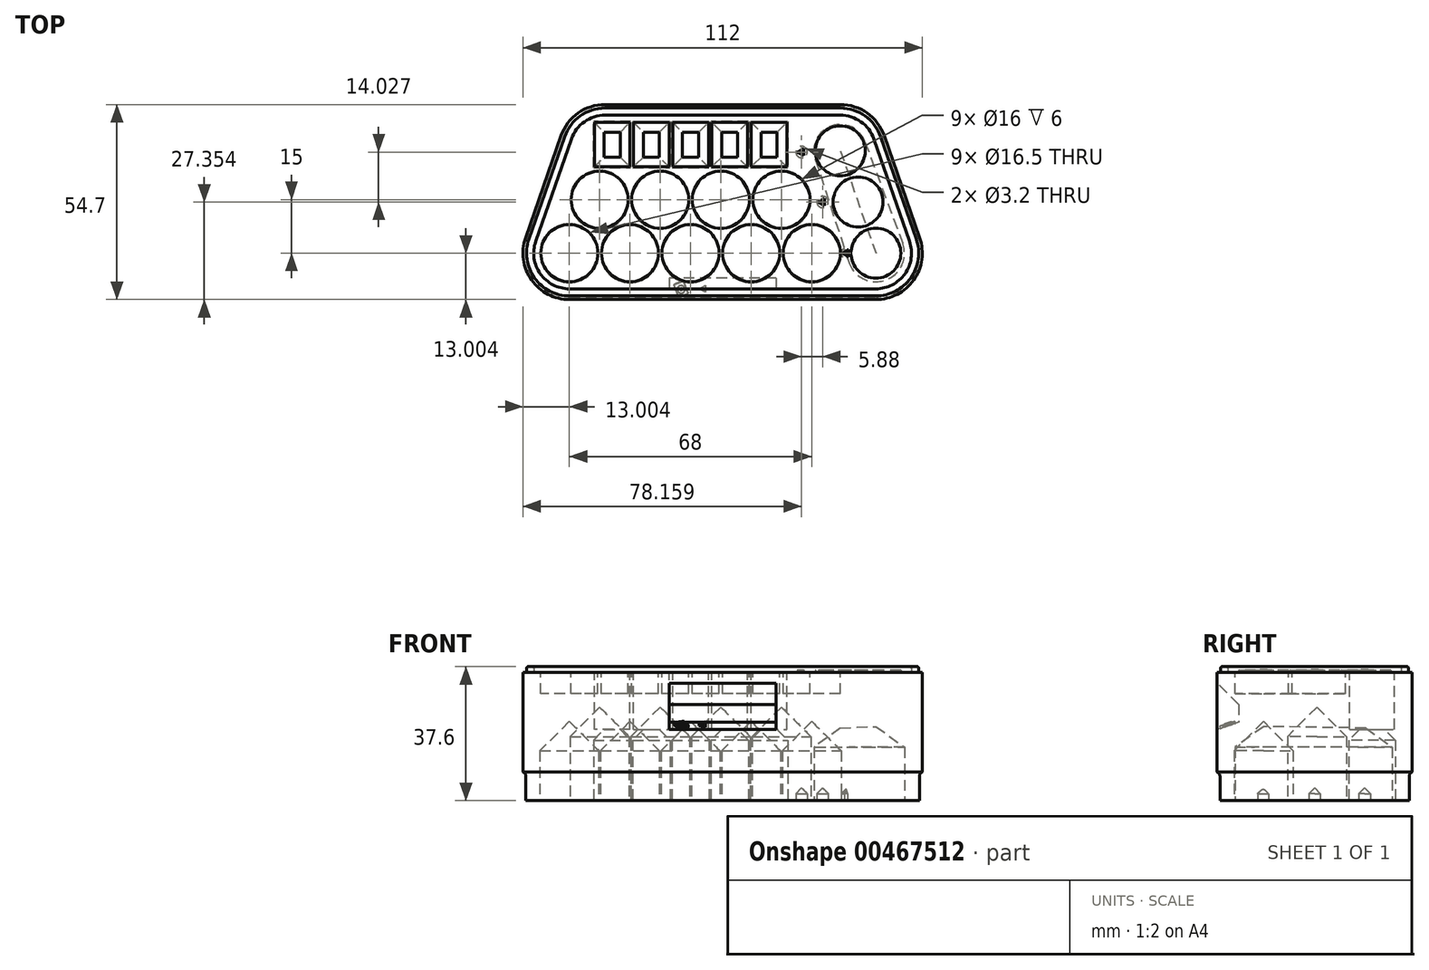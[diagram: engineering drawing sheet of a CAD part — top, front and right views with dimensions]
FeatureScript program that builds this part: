
annotation { "Feature Type Name" : "Feature", "Feature Type Description" : "" }
export const myFeature = defineFeature(function(context is Context, id is Id, definition is map)
    precondition{}
    {
        {
            var Q0;
            Q0=qCreatedBy(makeId("Top.planeOp"),FACE);
            var sketch = newSketch(context, id + "F0", { "sketchPlane" : qUnion([Q0])});
            skLineSegment(sketch, "E0", {"start": v(-9.05, 12.46) * mm, "end": v(-26.05, 12.46) * mm, "construction": true});
            skLineSegment(sketch, "E1", {"start": v(-26.05, 12.46) * mm, "end": v(-43.05, 12.46) * mm, "construction": true});
            skLineSegment(sketch, "E2", {"start": v(-9.05, 12.46) * mm, "end": v(7.95, 12.46) * mm, "construction": true});
            skLineSegment(sketch, "E3", {"start": v(7.95, 12.46) * mm, "end": v(24.95, 12.46) * mm, "construction": true});
            skLineSegment(sketch, "E4", {"start": v(-34.55, 27.46) * mm, "end": v(-17.55, 27.46) * mm, "construction": true});
            skPoint(sketch, "E4.endSnap0", {"position": v(-17.55, 12.46) * mm});
            skLineSegment(sketch, "E5", {"start": v(-17.55, 27.46) * mm, "end": v(-0.55, 27.46) * mm, "construction": true});
            skPoint(sketch, "E5.endSnap0", {"position": v(-0.55, 12.46) * mm});
            skLineSegment(sketch, "E6", {"start": v(-0.55, 27.46) * mm, "end": v(16.45, 27.46) * mm, "construction": true});
            skPoint(sketch, "E6.endSnap0", {"position": v(16.45, 12.46) * mm});
            skCircle(sketch, "E7", {"center": v(-43.05, 12.46) * mm, "radius": 8 * mm});
            skCircle(sketch, "E8", {"center": v(-26.05, 12.46) * mm, "radius": 8 * mm});
            skCircle(sketch, "E9", {"center": v(-9.05, 12.46) * mm, "radius": 8 * mm});
            skCircle(sketch, "E10", {"center": v(7.95, 12.46) * mm, "radius": 8 * mm});
            skCircle(sketch, "E11", {"center": v(24.95, 12.46) * mm, "radius": 8 * mm});
            skCircle(sketch, "E12", {"center": v(-34.55, 27.46) * mm, "radius": 8 * mm});
            skCircle(sketch, "E13", {"center": v(-17.55, 27.46) * mm, "radius": 8 * mm});
            skCircle(sketch, "E14", {"center": v(-0.55, 27.46) * mm, "radius": 8 * mm});
            skCircle(sketch, "E15", {"center": v(16.45, 27.46) * mm, "radius": 8 * mm});
            skLineSegment(sketch, "E16.top", {"start": v(-26.05, 49.16) * mm, "end": v(-36.05, 49.16) * mm});
            skLineSegment(sketch, "E16.left", {"start": v(-26.05, 36.66) * mm, "end": v(-26.05, 49.16) * mm});
            skLineSegment(sketch, "E16.right", {"start": v(-36.05, 36.66) * mm, "end": v(-36.05, 49.16) * mm});
            skArc(sketch, "E17", {"start": v(-55.32, 16.74) * mm, "mid": v(-53.64, 4.93) * mm, "end": v(-43.05, -0.54) * mm});
            skLineSegment(sketch, "E18", {"start": v(-45.32, 45.44) * mm, "end": v(-55.32, 16.74) * mm});
            skLineSegment(sketch, "E19", {"start": v(-43.05, -0.54) * mm, "end": v(42.95, -0.54) * mm});
            skLineSegment(sketch, "E20", {"start": v(32.95, 54.16) * mm, "end": v(-33.05, 54.16) * mm});
            skArc(sketch, "E21.trimOffspring", {"start": v(-33.05, 54.16) * mm, "mid": v(-40.58, 51.76) * mm, "end": v(-45.32, 45.44) * mm});
            skLineSegment(sketch, "E22", {"start": v(-43.05, 12.46) * mm, "end": v(-43.05, 19.46) * mm, "construction": true});
            skLineSegment(sketch, "E23", {"start": v(-36.05, 36.66) * mm, "end": v(-26.05, 36.66) * mm});
            skLineSegment(sketch, "E24", {"start": v(-34.55, 19.46) * mm, "end": v(16.45, 19.46) * mm, "construction": true});
            skLineSegment(sketch, "E25", {"start": v(-43.05, 20.46) * mm, "end": v(24.95, 20.46) * mm, "construction": true});
            skLineSegment(sketch, "E26", {"start": v(-26.05, 49.16) * mm, "end": v(-25.05, 49.16) * mm, "construction": true});
            skLineSegment(sketch, "E27.bottom", {"start": v(-25.05, 49.16) * mm, "end": v(-15.05, 49.16) * mm});
            skLineSegment(sketch, "E27.top", {"start": v(-25.05, 36.66) * mm, "end": v(-15.05, 36.66) * mm});
            skLineSegment(sketch, "E27.left", {"start": v(-25.05, 49.16) * mm, "end": v(-25.05, 36.66) * mm});
            skLineSegment(sketch, "E27.right", {"start": v(-15.05, 49.16) * mm, "end": v(-15.05, 36.66) * mm});
            skLineSegment(sketch, "E28", {"start": v(-15.05, 49.16) * mm, "end": v(-14.05, 49.16) * mm, "construction": true});
            skLineSegment(sketch, "E29.bottom", {"start": v(-14.05, 49.16) * mm, "end": v(-4.05, 49.16) * mm});
            skLineSegment(sketch, "E29.top", {"start": v(-14.05, 36.66) * mm, "end": v(-4.05, 36.66) * mm});
            skLineSegment(sketch, "E29.left", {"start": v(-14.05, 49.16) * mm, "end": v(-14.05, 36.66) * mm});
            skLineSegment(sketch, "E29.right", {"start": v(-4.05, 49.16) * mm, "end": v(-4.05, 36.66) * mm});
            skLineSegment(sketch, "E30", {"start": v(-4.05, 49.16) * mm, "end": v(-3.05, 49.16) * mm, "construction": true});
            skLineSegment(sketch, "E31.left", {"start": v(-3.05, 49.16) * mm, "end": v(-3.05, 36.66) * mm});
            skLineSegment(sketch, "E31.right", {"start": v(7.95, 49.16) * mm, "end": v(7.95, 36.66) * mm});
            skLineSegment(sketch, "E32.left", {"start": v(6.95, 49.16) * mm, "end": v(6.95, 36.66) * mm});
            skLineSegment(sketch, "E32.right", {"start": v(17.95, 49.16) * mm, "end": v(17.95, 36.66) * mm});
            skLineSegment(sketch, "E33", {"start": v(-3.05, 36.66) * mm, "end": v(6.95, 36.66) * mm});
            skLineSegment(sketch, "E34", {"start": v(7.95, 36.66) * mm, "end": v(17.95, 36.66) * mm});
            skPoint(sketch, "E35", {"position": v(-9.05, 49.16) * mm});
            skLineSegment(sketch, "E36", {"start": v(7.95, 49.16) * mm, "end": v(17.95, 49.16) * mm});
            skLineSegment(sketch, "E37", {"start": v(6.95, 49.16) * mm, "end": v(-3.05, 49.16) * mm});
            skLineSegment(sketch, "E38", {"start": v(6.95, 49.16) * mm, "end": v(7.95, 49.16) * mm, "construction": true});
            skLineSegment(sketch, "E39", {"start": v(45.23, 45.44) * mm, "end": v(55.23, 16.74) * mm});
            skArc(sketch, "E40.trimOffspring", {"start": v(45.23, 45.44) * mm, "mid": v(40.48, 51.76) * mm, "end": v(32.95, 54.16) * mm});
            skArc(sketch, "E41.trimOffspring", {"start": v(42.95, -0.54) * mm, "mid": v(53.55, 4.93) * mm, "end": v(55.23, 16.74) * mm});
            skLineSegment(sketch, "E42", {"start": v(-34.55, 27.46) * mm, "end": v(-34.55, 35.46) * mm, "construction": true});
            skLineSegment(sketch, "E43", {"start": v(-34.55, 35.46) * mm, "end": v(-34.55, 36.66) * mm, "construction": true});
            skLineSegment(sketch, "E44", {"start": v(-33.05, 41.16) * mm, "end": v(14.95, 41.16) * mm, "construction": true});
            skLineSegment(sketch, "E45", {"start": v(-9.05, 41.16) * mm, "end": v(-9.05, 12.46) * mm, "construction": true});
            skCircle(sketch, "E46", {"center": v(42.95, 12.46) * mm, "radius": 7 * mm});
            skCircle(sketch, "E47", {"center": v(32.95, 41.16) * mm, "radius": 7 * mm});
            skPoint(sketch, "E47.centerSnap0", {"position": v(17.95, 42.91) * mm});
            skLineSegment(sketch, "E48", {"start": v(32.95, 41.16) * mm, "end": v(42.95, 12.46) * mm, "construction": true});
            skCircle(sketch, "E49", {"center": v(37.95, 26.81) * mm, "radius": 7 * mm});
            skLineSegment(sketch, "E50", {"start": v(42.95, 12.46) * mm, "end": v(32.95, 12.46) * mm, "construction": true});
            skLineSegment(sketch, "E51", {"start": v(27.95, 40.84) * mm, "end": v(17.95, 40.84) * mm, "construction": true});
            skLineSegment(sketch, "E52", {"start": v(20.95, 40.84) * mm, "end": v(22.69, 41.84) * mm});
            skLineSegment(sketch, "E53", {"start": v(22.69, 41.84) * mm, "end": v(22.69, 39.84) * mm});
            skLineSegment(sketch, "E54", {"start": v(22.69, 39.84) * mm, "end": v(20.95, 40.84) * mm});
            skLineSegment(sketch, "E55", {"start": v(26.83, 26.81) * mm, "end": v(28.57, 27.81) * mm});
            skLineSegment(sketch, "E56", {"start": v(28.57, 27.81) * mm, "end": v(28.57, 25.81) * mm});
            skLineSegment(sketch, "E57", {"start": v(28.57, 25.81) * mm, "end": v(26.83, 26.81) * mm});
            skLineSegment(sketch, "E58", {"start": v(33.7, 12.46) * mm, "end": v(35.44, 13.46) * mm});
            skLineSegment(sketch, "E59", {"start": v(35.44, 13.46) * mm, "end": v(35.44, 11.46) * mm});
            skLineSegment(sketch, "E60", {"start": v(35.44, 11.46) * mm, "end": v(33.7, 12.46) * mm});
            skLineSegment(sketch, "E61", {"start": v(-55.32, 16.74) * mm, "end": v(-55.32, 45.44) * mm, "construction": true});
            skLineSegment(sketch, "E62", {"start": v(-55.32, 45.44) * mm, "end": v(-45.32, 45.44) * mm, "construction": true});
            skLineSegment(sketch, "E63", {"start": v(45.23, 45.44) * mm, "end": v(55.23, 45.44) * mm, "construction": true});
            skLineSegment(sketch, "E64", {"start": v(55.23, 45.44) * mm, "end": v(55.23, 16.74) * mm, "construction": true});
            skLineSegment(sketch, "E65", {"start": v(-43.05, -0.54) * mm, "end": v(-43.05, 4.46) * mm, "construction": true});
            skSolve(sketch);
        }
        {
            var Q0;
            Q0=makeQuery(id+"F0.imprint","IMPRINT",FACE,{"disambiguationData":[TD([[makeQuery(id+"F0.imprint","IMPRINT",EDGE,{"derivedFrom":sQuery(id+"F0.wireOp",EDGE,"E12")}),1.0]])]});
            var Q1;
            Q1=makeQuery(id+"F0.imprint","IMPRINT",FACE,{"disambiguationData":[TD([[makeQuery(id+"F0.imprint","IMPRINT",EDGE,{"derivedFrom":sQuery(id+"F0.wireOp",EDGE,"E13")}),1.0]])]});
            var Q2;
            Q2=makeQuery(id+"F0.imprint","IMPRINT",FACE,{"disambiguationData":[TD([[makeQuery(id+"F0.imprint","IMPRINT",EDGE,{"derivedFrom":sQuery(id+"F0.wireOp",EDGE,"E14")}),1.0]])]});
            var Q3;
            Q3=makeQuery(id+"F0.imprint","IMPRINT",FACE,{"disambiguationData":[TD([[makeQuery(id+"F0.imprint","IMPRINT",EDGE,{"derivedFrom":sQuery(id+"F0.wireOp",EDGE,"E15")}),1.0]])]});
            var Q4;
            Q4=makeQuery(id+"F0.imprint","IMPRINT",FACE,{"disambiguationData":[TD([[makeQuery(id+"F0.imprint","IMPRINT",EDGE,{"derivedFrom":sQuery(id+"F0.wireOp",EDGE,"E31.right")}),1.0]])]});
            var Q5;
            Q5=makeQuery(id+"F0.imprint","IMPRINT",FACE,{"disambiguationData":[TD([[makeQuery(id+"F0.imprint","IMPRINT",EDGE,{"derivedFrom":sQuery(id+"F0.wireOp",EDGE,"E31.left")}),1.0]])]});
            var Q6;
            Q6=makeQuery(id+"F0.imprint","IMPRINT",FACE,{"disambiguationData":[TD([[makeQuery(id+"F0.imprint","IMPRINT",EDGE,{"derivedFrom":sQuery(id+"F0.wireOp",EDGE,"E29.bottom")}),-1.0]])]});
            var Q7;
            Q7=makeQuery(id+"F0.imprint","IMPRINT",FACE,{"disambiguationData":[TD([[makeQuery(id+"F0.imprint","IMPRINT",EDGE,{"derivedFrom":sQuery(id+"F0.wireOp",EDGE,"E27.bottom")}),-1.0]])]});
            var Q8;
            Q8=makeQuery(id+"F0.imprint","IMPRINT",FACE,{"disambiguationData":[TD([[makeQuery(id+"F0.imprint","IMPRINT",EDGE,{"derivedFrom":sQuery(id+"F0.wireOp",EDGE,"E16.top")}),1.0]])]});
            var Q9;
            Q9=makeQuery(id+"F0.imprint","IMPRINT",FACE,{"disambiguationData":[TD([[makeQuery(id+"F0.imprint","IMPRINT",EDGE,{"derivedFrom":sQuery(id+"F0.wireOp",EDGE,"E8")}),1.0]])]});
            var Q10;
            Q10=makeQuery(id+"F0.imprint","IMPRINT",FACE,{"disambiguationData":[TD([[makeQuery(id+"F0.imprint","IMPRINT",EDGE,{"derivedFrom":sQuery(id+"F0.wireOp",EDGE,"E9")}),1.0]])]});
            var Q11;
            Q11=makeQuery(id+"F0.imprint","IMPRINT",FACE,{"disambiguationData":[TD([[makeQuery(id+"F0.imprint","IMPRINT",EDGE,{"derivedFrom":sQuery(id+"F0.wireOp",EDGE,"E10")}),1.0]])]});
            var Q12;
            Q12=makeQuery(id+"F0.imprint","IMPRINT",FACE,{"disambiguationData":[TD([[makeQuery(id+"F0.imprint","IMPRINT",EDGE,{"derivedFrom":sQuery(id+"F0.wireOp",EDGE,"E11")}),1.0]])]});
            var Q13;
            Q13=makeQuery(id+"F0.imprint","IMPRINT",FACE,{"disambiguationData":[TD([[makeQuery(id+"F0.imprint","IMPRINT",EDGE,{"derivedFrom":sQuery(id+"F0.wireOp",EDGE,"E7")}),1.0]])]});
            var Q14;
            Q14=makeQuery(id+"F0.imprint","IMPRINT",FACE,{"disambiguationData":[TD([[makeQuery(id+"F0.imprint","IMPRINT",EDGE,{"derivedFrom":sQuery(id+"F0.wireOp",EDGE,"E47")}),1.0]])]});
            var Q15;
            Q15=makeQuery(id+"F0.imprint","IMPRINT",FACE,{"disambiguationData":[TD([[makeQuery(id+"F0.imprint","IMPRINT",EDGE,{"derivedFrom":sQuery(id+"F0.wireOp",EDGE,"E49")}),1.0]])]});
            var Q16;
            Q16=makeQuery(id+"F0.imprint","IMPRINT",FACE,{"disambiguationData":[TD([[makeQuery(id+"F0.imprint","IMPRINT",EDGE,{"derivedFrom":sQuery(id+"F0.wireOp",EDGE,"E46")}),1.0]])]});
            var Q17;
            Q17=makeQuery(id+"F0.imprint","IMPRINT",FACE,{"disambiguationData":[TD([[makeQuery(id+"F0.imprint","IMPRINT",EDGE,{"derivedFrom":sQuery(id+"F0.wireOp",EDGE,"E52")}),-1.0]])]});
            var Q18;
            Q18=makeQuery(id+"F0.imprint","IMPRINT",FACE,{"disambiguationData":[TD([[makeQuery(id+"F0.imprint","IMPRINT",EDGE,{"derivedFrom":sQuery(id+"F0.wireOp",EDGE,"E55")}),-1.0]])]});
            var Q19;
            Q19=makeQuery(id+"F0.imprint","IMPRINT",FACE,{"disambiguationData":[TD([[makeQuery(id+"F0.imprint","IMPRINT",EDGE,{"derivedFrom":sQuery(id+"F0.wireOp",EDGE,"E7")}),-1.0]])]});
            var Q20;
            Q20=makeQuery(id+"F0.imprint","IMPRINT",FACE,{"disambiguationData":[TD([[makeQuery(id+"F0.imprint","IMPRINT",EDGE,{"derivedFrom":sQuery(id+"F0.wireOp",EDGE,"E58")}),-1.0]])]});
            extrude(context, id + "F1", {"entities" : qUnion([Q0, Q1, Q2, Q3, Q4, Q5, Q6, Q7, Q8, Q9, Q10, Q11, Q12, Q13, Q14, Q15, Q16, Q17, Q18, Q19, Q20]), "oppositeDirection" : true, "depth" : 36 * mm});
        }
        {
            var Q0;
            Q0=makeQuery(id+"F0.imprint","IMPRINT",FACE,{"disambiguationData":[TD([[makeQuery(id+"F0.imprint","IMPRINT",EDGE,{"derivedFrom":sQuery(id+"F0.wireOp",EDGE,"E11")}),1.0]])]});
            var Q1;
            Q1=makeQuery(id+"F0.imprint","IMPRINT",FACE,{"disambiguationData":[TD([[makeQuery(id+"F0.imprint","IMPRINT",EDGE,{"derivedFrom":sQuery(id+"F0.wireOp",EDGE,"E10")}),1.0]])]});
            var Q2;
            Q2=makeQuery(id+"F0.imprint","IMPRINT",FACE,{"disambiguationData":[TD([[makeQuery(id+"F0.imprint","IMPRINT",EDGE,{"derivedFrom":sQuery(id+"F0.wireOp",EDGE,"E9")}),1.0]])]});
            var Q3;
            Q3=makeQuery(id+"F0.imprint","IMPRINT",FACE,{"disambiguationData":[TD([[makeQuery(id+"F0.imprint","IMPRINT",EDGE,{"derivedFrom":sQuery(id+"F0.wireOp",EDGE,"E8")}),1.0]])]});
            var Q4;
            Q4=makeQuery(id+"F0.imprint","IMPRINT",FACE,{"disambiguationData":[TD([[makeQuery(id+"F0.imprint","IMPRINT",EDGE,{"derivedFrom":sQuery(id+"F0.wireOp",EDGE,"E7")}),1.0]])]});
            extrude(context, id + "F2", {"entities" : qUnion([Q0, Q1, Q2, Q3, Q4]), "operationType" : NewBodyOperationType.REMOVE, "oppositeDirection" : true, "depth" : 6 * mm});
        }
        {
            var Q0;
            Q0=makeQuery(id+"F0.imprint","IMPRINT",FACE,{"disambiguationData":[TD([[makeQuery(id+"F0.imprint","IMPRINT",EDGE,{"derivedFrom":sQuery(id+"F0.wireOp",EDGE,"E15")}),1.0]])]});
            var Q1;
            Q1=makeQuery(id+"F0.imprint","IMPRINT",FACE,{"disambiguationData":[TD([[makeQuery(id+"F0.imprint","IMPRINT",EDGE,{"derivedFrom":sQuery(id+"F0.wireOp",EDGE,"E14")}),1.0]])]});
            var Q2;
            Q2=makeQuery(id+"F0.imprint","IMPRINT",FACE,{"disambiguationData":[TD([[makeQuery(id+"F0.imprint","IMPRINT",EDGE,{"derivedFrom":sQuery(id+"F0.wireOp",EDGE,"E13")}),1.0]])]});
            var Q3;
            Q3=makeQuery(id+"F0.imprint","IMPRINT",FACE,{"disambiguationData":[TD([[makeQuery(id+"F0.imprint","IMPRINT",EDGE,{"derivedFrom":sQuery(id+"F0.wireOp",EDGE,"E12")}),1.0]])]});
            extrude(context, id + "F3", {"entities" : qUnion([Q0, Q1, Q2, Q3]), "operationType" : NewBodyOperationType.REMOVE, "oppositeDirection" : true, "depth" : 6 * mm});
        }
        {
            var Q0;
            Q0=makeQuery(id+"F0.imprint","IMPRINT",FACE,{"disambiguationData":[TD([[makeQuery(id+"F0.imprint","IMPRINT",EDGE,{"derivedFrom":sQuery(id+"F0.wireOp",EDGE,"E31.right")}),1.0]])]});
            var Q1;
            Q1=makeQuery(id+"F0.imprint","IMPRINT",FACE,{"disambiguationData":[TD([[makeQuery(id+"F0.imprint","IMPRINT",EDGE,{"derivedFrom":sQuery(id+"F0.wireOp",EDGE,"E31.left")}),1.0]])]});
            var Q2;
            Q2=makeQuery(id+"F0.imprint","IMPRINT",FACE,{"disambiguationData":[TD([[makeQuery(id+"F0.imprint","IMPRINT",EDGE,{"derivedFrom":sQuery(id+"F0.wireOp",EDGE,"E29.bottom")}),-1.0]])]});
            var Q3;
            Q3=makeQuery(id+"F0.imprint","IMPRINT",FACE,{"disambiguationData":[TD([[makeQuery(id+"F0.imprint","IMPRINT",EDGE,{"derivedFrom":sQuery(id+"F0.wireOp",EDGE,"E27.bottom")}),-1.0]])]});
            var Q4;
            Q4=makeQuery(id+"F0.imprint","IMPRINT",FACE,{"disambiguationData":[TD([[makeQuery(id+"F0.imprint","IMPRINT",EDGE,{"derivedFrom":sQuery(id+"F0.wireOp",EDGE,"E16.top")}),1.0]])]});
            extrude(context, id + "F4", {"entities" : qUnion([Q0, Q1, Q2, Q3, Q4]), "operationType" : NewBodyOperationType.REMOVE, "oppositeDirection" : true, "depth" : 16 * mm});
        }
        {
            var Q0;
            Q0=makeQuery(id+"F0.imprint","IMPRINT",FACE,{"disambiguationData":[TD([[makeQuery(id+"F0.imprint","IMPRINT",EDGE,{"derivedFrom":sQuery(id+"F0.wireOp",EDGE,"E7")}),-1.0]])]});
            var sketch = newSketch(context, id + "F5", { "sketchPlane" : qUnion([Q0])});
            skLineSegment(sketch, "E66.1", {"start": v(44.29, 45.11) * mm, "end": v(54.29, 16.41) * mm});
            skLineSegment(sketch, "E66.2", {"start": v(32.95, 53.16) * mm, "end": v(-33.05, 53.16) * mm});
            skArc(sketch, "E66.3", {"start": v(42.95, 0.46) * mm, "mid": v(52.74, 5.51) * mm, "end": v(54.29, 16.41) * mm});
            skArc(sketch, "E66.4", {"start": v(-33.05, 53.16) * mm, "mid": v(-40, 50.95) * mm, "end": v(-44.38, 45.11) * mm});
            skLineSegment(sketch, "E66.5", {"start": v(-44.38, 45.11) * mm, "end": v(-54.38, 16.41) * mm});
            skArc(sketch, "E66.6", {"start": v(-54.38, 16.41) * mm, "mid": v(-52.83, 5.51) * mm, "end": v(-43.05, 0.46) * mm});
            skLineSegment(sketch, "E66.7", {"start": v(-43.05, 0.46) * mm, "end": v(42.95, 0.46) * mm});
            skLineSegment(sketch, "E67.1", {"start": v(42.4, 44.45) * mm, "end": v(52.4, 15.75) * mm});
            skLineSegment(sketch, "E67.2", {"start": v(32.95, 51.16) * mm, "end": v(-33.05, 51.16) * mm});
            skArc(sketch, "E67.3", {"start": v(42.95, 2.46) * mm, "mid": v(51.1, 6.67) * mm, "end": v(52.4, 15.75) * mm});
            skArc(sketch, "E67.4", {"start": v(-33.05, 51.16) * mm, "mid": v(-38.84, 49.32) * mm, "end": v(-42.49, 44.45) * mm});
            skLineSegment(sketch, "E67.5", {"start": v(-42.49, 44.45) * mm, "end": v(-52.49, 15.75) * mm});
            skArc(sketch, "E67.6", {"start": v(-52.49, 15.75) * mm, "mid": v(-51.2, 6.67) * mm, "end": v(-43.05, 2.46) * mm});
            skLineSegment(sketch, "E67.7", {"start": v(-43.05, 2.46) * mm, "end": v(42.95, 2.46) * mm});
            skArc(sketch, "E68.0", {"start": v(44.29, 45.11) * mm, "mid": v(39.9, 50.95) * mm, "end": v(32.95, 53.16) * mm});
            skArc(sketch, "E69.0", {"start": v(42.4, 44.45) * mm, "mid": v(38.75, 49.32) * mm, "end": v(32.95, 51.16) * mm});
            skSolve(sketch);
        }
        {
            var Q0;
            Q0=makeQuery(id+"F5.imprint","IMPRINT",FACE,{"disambiguationData":[TD([[makeQuery(id+"F5.imprint","IMPRINT",EDGE,{"derivedFrom":sQuery(id+"F5.wireOp",EDGE,"E66.1")}),-1.0]])]});
            extrude(context, id + "F6", {"entities" : qUnion([Q0]), "operationType" : NewBodyOperationType.ADD, "depth" : 1.6 * mm, "offsetDistance" : 25 * mm});
        }
        {
            var Q0;
            Q0=makeQuery(id+"F1.opExtrude","CAP_FACE",FACE,{"disambiguationData":[OSD([sQuery(id+"F0.wireOp",EDGE,"E17"),sQuery(id+"F0.wireOp",EDGE,"E18"),sQuery(id+"F0.wireOp",EDGE,"E19"),sQuery(id+"F0.wireOp",EDGE,"ED3TIhDh-ExMu-AOSy-Hj7E-wzorArON6frA"),sQuery(id+"F0.wireOp",EDGE,"E20"),sQuery(id+"F0.wireOp",EDGE,"E21.trimOffspring")])],"isStart":false});
            var sketch = newSketch(context, id + "F7", { "sketchPlane" : qUnion([Q0])});
            skArc(sketch, "E70.0", {"start": v(-54.57, -16.48) * mm, "mid": v(-53, -5.4) * mm, "end": v(-43.05, -0.26) * mm});
            skLineSegment(sketch, "E70.1", {"start": v(-44.57, -45.18) * mm, "end": v(-54.57, -16.48) * mm});
            skLineSegment(sketch, "E70.2", {"start": v(-43.05, -0.26) * mm, "end": v(42.95, -0.26) * mm});
            skArc(sketch, "E70.3", {"start": v(-33.05, -53.36) * mm, "mid": v(-40.11, -51.1) * mm, "end": v(-44.57, -45.18) * mm});
            skArc(sketch, "E70.4", {"start": v(42.95, -0.26) * mm, "mid": v(52.9, -5.4) * mm, "end": v(54.47, -16.48) * mm});
            skLineSegment(sketch, "E70.5", {"start": v(44.47, -45.18) * mm, "end": v(54.47, -16.48) * mm});
            skLineSegment(sketch, "E70.7", {"start": v(32.95, -53.36) * mm, "end": v(-33.05, -53.36) * mm});
            skArc(sketch, "E71.0", {"start": v(-52.3, -15.69) * mm, "mid": v(-51.03, -6.79) * mm, "end": v(-43.05, -2.66) * mm});
            skLineSegment(sketch, "E71.1", {"start": v(-42.3, -44.39) * mm, "end": v(-52.3, -15.69) * mm});
            skLineSegment(sketch, "E71.2", {"start": v(-43.05, -2.66) * mm, "end": v(42.95, -2.66) * mm});
            skArc(sketch, "E71.3", {"start": v(-33.05, -50.96) * mm, "mid": v(-38.72, -49.15) * mm, "end": v(-42.3, -44.39) * mm});
            skArc(sketch, "E71.4", {"start": v(42.95, -2.66) * mm, "mid": v(50.94, -6.79) * mm, "end": v(52.2, -15.69) * mm});
            skLineSegment(sketch, "E71.5", {"start": v(42.2, -44.39) * mm, "end": v(52.2, -15.69) * mm});
            skLineSegment(sketch, "E71.7", {"start": v(32.95, -50.96) * mm, "end": v(-33.05, -50.96) * mm});
            skArc(sketch, "E72.0", {"start": v(44.47, -45.18) * mm, "mid": v(40.02, -51.1) * mm, "end": v(32.95, -53.36) * mm});
            skArc(sketch, "E73.0", {"start": v(42.2, -44.39) * mm, "mid": v(38.63, -49.15) * mm, "end": v(32.95, -50.96) * mm});
            skSolve(sketch);
        }
        {
            var Q0;
            Q0=makeQuery(id+"F7.imprint","IMPRINT",FACE,{"disambiguationData":[TD([[makeQuery(id+"F7.imprint","IMPRINT",EDGE,{"derivedFrom":sQuery(id+"F7.wireOp",EDGE,"E70.0")}),-1.0]])]});
            extrude(context, id + "F8", {"entities" : qUnion([Q0]), "operationType" : NewBodyOperationType.REMOVE, "oppositeDirection" : true, "depth" : 8 * mm, "offsetDistance" : 25 * mm});
        }
        {
            var Q0;
            Q0=makeQuery(id+"F8.boolean.opBoolean","SPLIT",FACE,{"disambiguationData":[TD([makeQuery(id+"F8.opExtrude","SWEPT_FACE",FACE,{"disambiguationData":[OSD([sQuery(id+"F7.wireOp",EDGE,"E71.0")])]})])],"derivedFrom":makeQuery(id+"F1.opExtrude","CAP_FACE",FACE,{"disambiguationData":[OSD([sQuery(id+"F0.wireOp",EDGE,"E17"),sQuery(id+"F0.wireOp",EDGE,"E18"),sQuery(id+"F0.wireOp",EDGE,"E19"),sQuery(id+"F0.wireOp",EDGE,"E20"),sQuery(id+"F0.wireOp",EDGE,"E21.trimOffspring"),sQuery(id+"F0.wireOp",EDGE,"E39"),sQuery(id+"F0.wireOp",EDGE,"E40.trimOffspring"),sQuery(id+"F0.wireOp",EDGE,"E41.trimOffspring")])],"isStart":false})});
            var sketch = newSketch(context, id + "F9", { "sketchPlane" : qUnion([Q0])});
            skLineSegment(sketch, "E74.0", {"start": v(-36.05, -36.66) * mm, "end": v(-36.05, -49.16) * mm, "construction": true});
            skLineSegment(sketch, "E75.0", {"start": v(-36.05, -36.66) * mm, "end": v(-26.05, -36.66) * mm, "construction": true});
            skLineSegment(sketch, "E76.0", {"start": v(-25.05, -36.66) * mm, "end": v(-15.05, -36.66) * mm, "construction": true});
            skLineSegment(sketch, "E77.0", {"start": v(-14.05, -36.66) * mm, "end": v(-4.05, -36.66) * mm, "construction": true});
            skLineSegment(sketch, "E78.0", {"start": v(-3.05, -36.66) * mm, "end": v(6.95, -36.66) * mm, "construction": true});
            skLineSegment(sketch, "E79.0", {"start": v(7.95, -36.66) * mm, "end": v(17.95, -36.66) * mm, "construction": true});
            skLineSegment(sketch, "E80.0", {"start": v(7.95, -49.16) * mm, "end": v(17.95, -49.16) * mm, "construction": true});
            skLineSegment(sketch, "E81.0", {"start": v(6.95, -49.16) * mm, "end": v(-3.05, -49.16) * mm, "construction": true});
            skLineSegment(sketch, "E82.0", {"start": v(-14.05, -49.16) * mm, "end": v(-4.05, -49.16) * mm, "construction": true});
            skLineSegment(sketch, "E83.0", {"start": v(-25.05, -49.16) * mm, "end": v(-15.05, -49.16) * mm, "construction": true});
            skLineSegment(sketch, "E84.0", {"start": v(-26.05, -49.16) * mm, "end": v(-36.05, -49.16) * mm, "construction": true});
            skLineSegment(sketch, "E85.0", {"start": v(-26.05, -36.66) * mm, "end": v(-26.05, -49.16) * mm, "construction": true});
            skLineSegment(sketch, "E86.0", {"start": v(-25.05, -49.16) * mm, "end": v(-25.05, -36.66) * mm, "construction": true});
            skLineSegment(sketch, "E87.0", {"start": v(-15.05, -49.16) * mm, "end": v(-15.05, -36.66) * mm, "construction": true});
            skLineSegment(sketch, "E88.0", {"start": v(-14.05, -49.16) * mm, "end": v(-14.05, -36.66) * mm, "construction": true});
            skLineSegment(sketch, "E89.0", {"start": v(-4.05, -49.16) * mm, "end": v(-4.05, -36.66) * mm, "construction": true});
            skLineSegment(sketch, "E90.0", {"start": v(-3.05, -49.16) * mm, "end": v(-3.05, -36.66) * mm, "construction": true});
            skLineSegment(sketch, "E91.0", {"start": v(6.95, -49.16) * mm, "end": v(6.95, -36.66) * mm, "construction": true});
            skLineSegment(sketch, "E92.0", {"start": v(7.95, -49.16) * mm, "end": v(7.95, -36.66) * mm, "construction": true});
            skLineSegment(sketch, "E93.0", {"start": v(17.95, -49.16) * mm, "end": v(17.95, -36.66) * mm, "construction": true});
            skPoint(sketch, "E94.0", {"position": v(-43.05, -12.46) * mm});
            skPoint(sketch, "E95.0", {"position": v(-34.55, -27.46) * mm});
            skPoint(sketch, "E96.0", {"position": v(-26.05, -12.46) * mm});
            skPoint(sketch, "E97.0", {"position": v(-17.55, -27.46) * mm});
            skPoint(sketch, "E98.0", {"position": v(-0.55, -27.46) * mm});
            skPoint(sketch, "E99.0", {"position": v(-9.05, -12.46) * mm});
            skPoint(sketch, "E100.0", {"position": v(16.45, -27.46) * mm});
            skPoint(sketch, "E101.0", {"position": v(7.95, -12.46) * mm});
            skPoint(sketch, "E102.0", {"position": v(24.95, -12.46) * mm});
            skCircle(sketch, "E103", {"center": v(-43.05, -12.46) * mm, "radius": 8.25 * mm});
            skCircle(sketch, "E104", {"center": v(-26.05, -12.46) * mm, "radius": 8.25 * mm});
            skCircle(sketch, "E105", {"center": v(-9.05, -12.46) * mm, "radius": 8.25 * mm});
            skCircle(sketch, "E106", {"center": v(7.95, -12.46) * mm, "radius": 8.25 * mm});
            skCircle(sketch, "E107", {"center": v(24.95, -12.46) * mm, "radius": 8.25 * mm});
            skCircle(sketch, "E108", {"center": v(16.45, -27.46) * mm, "radius": 8.25 * mm});
            skCircle(sketch, "E109", {"center": v(-0.55, -27.46) * mm, "radius": 8.25 * mm});
            skCircle(sketch, "E110", {"center": v(-17.55, -27.46) * mm, "radius": 8.25 * mm});
            skCircle(sketch, "E111", {"center": v(-34.55, -27.46) * mm, "radius": 8.25 * mm});
            skLineSegment(sketch, "E112.0", {"start": v(-36.3, -36.41) * mm, "end": v(-25.8, -36.41) * mm});
            skLineSegment(sketch, "E112.1", {"start": v(-36.3, -36.41) * mm, "end": v(-36.3, -49.41) * mm});
            skLineSegment(sketch, "E112.2", {"start": v(-25.8, -49.41) * mm, "end": v(-36.3, -49.41) * mm});
            skLineSegment(sketch, "E112.3", {"start": v(-25.8, -36.41) * mm, "end": v(-25.8, -49.41) * mm});
            skLineSegment(sketch, "E113.0", {"start": v(-25.3, -49.41) * mm, "end": v(-25.3, -36.41) * mm});
            skLineSegment(sketch, "E113.1", {"start": v(-25.3, -49.41) * mm, "end": v(-14.8, -49.41) * mm});
            skLineSegment(sketch, "E113.2", {"start": v(-14.8, -49.41) * mm, "end": v(-14.8, -36.41) * mm});
            skLineSegment(sketch, "E113.3", {"start": v(-25.3, -36.41) * mm, "end": v(-14.8, -36.41) * mm});
            skLineSegment(sketch, "E114.0", {"start": v(-14.3, -49.41) * mm, "end": v(-14.3, -36.41) * mm});
            skLineSegment(sketch, "E114.1", {"start": v(-14.3, -49.41) * mm, "end": v(-3.8, -49.41) * mm});
            skLineSegment(sketch, "E114.2", {"start": v(-3.8, -49.41) * mm, "end": v(-3.8, -36.41) * mm});
            skLineSegment(sketch, "E114.3", {"start": v(-14.3, -36.41) * mm, "end": v(-3.8, -36.41) * mm});
            skLineSegment(sketch, "E115.0", {"start": v(-3.3, -49.41) * mm, "end": v(-3.3, -36.41) * mm});
            skLineSegment(sketch, "E115.1", {"start": v(7.2, -49.41) * mm, "end": v(-3.3, -49.41) * mm});
            skLineSegment(sketch, "E115.2", {"start": v(7.2, -49.41) * mm, "end": v(7.2, -36.41) * mm});
            skLineSegment(sketch, "E115.3", {"start": v(-3.3, -36.41) * mm, "end": v(7.2, -36.41) * mm});
            skLineSegment(sketch, "E116.0", {"start": v(7.7, -49.41) * mm, "end": v(7.7, -36.41) * mm});
            skLineSegment(sketch, "E116.1", {"start": v(7.7, -49.41) * mm, "end": v(18.2, -49.41) * mm});
            skLineSegment(sketch, "E116.2", {"start": v(18.2, -49.41) * mm, "end": v(18.2, -36.41) * mm});
            skLineSegment(sketch, "E116.3", {"start": v(7.7, -36.41) * mm, "end": v(18.2, -36.41) * mm});
            skSolve(sketch);
        }
        {
            var Q0;
            Q0=makeQuery(id+"F9.imprint","IMPRINT",FACE,{"disambiguationData":[TD([[makeQuery(id+"F9.imprint","IMPRINT",EDGE,{"derivedFrom":sQuery(id+"F9.wireOp",EDGE,"E107")}),1.0]])]});
            var Q1;
            Q1=makeQuery(id+"F9.imprint","IMPRINT",FACE,{"disambiguationData":[TD([[makeQuery(id+"F9.imprint","IMPRINT",EDGE,{"derivedFrom":sQuery(id+"F9.wireOp",EDGE,"E106")}),1.0]])]});
            var Q2;
            Q2=makeQuery(id+"F9.imprint","IMPRINT",FACE,{"disambiguationData":[TD([[makeQuery(id+"F9.imprint","IMPRINT",EDGE,{"derivedFrom":sQuery(id+"F9.wireOp",EDGE,"E105")}),1.0]])]});
            var Q3;
            Q3=makeQuery(id+"F9.imprint","IMPRINT",FACE,{"disambiguationData":[TD([[makeQuery(id+"F9.imprint","IMPRINT",EDGE,{"derivedFrom":sQuery(id+"F9.wireOp",EDGE,"E104")}),1.0]])]});
            var Q4;
            Q4=makeQuery(id+"F9.imprint","IMPRINT",FACE,{"disambiguationData":[TD([[makeQuery(id+"F9.imprint","IMPRINT",EDGE,{"derivedFrom":sQuery(id+"F9.wireOp",EDGE,"E103")}),1.0]])]});
            extrude(context, id + "F10", {"entities" : qUnion([Q0, Q1, Q2, Q3, Q4]), "operationType" : NewBodyOperationType.REMOVE, "oppositeDirection" : true, "depth" : 14 * mm});
        }
        {
            var Q0;
            Q0=makeQuery(id+"F9.imprint","IMPRINT",FACE,{"disambiguationData":[TD([[makeQuery(id+"F9.imprint","IMPRINT",EDGE,{"derivedFrom":sQuery(id+"F9.wireOp",EDGE,"E112.0")}),-1.0]])]});
            var Q1;
            Q1=makeQuery(id+"F9.imprint","IMPRINT",FACE,{"disambiguationData":[TD([[makeQuery(id+"F9.imprint","IMPRINT",EDGE,{"derivedFrom":sQuery(id+"F9.wireOp",EDGE,"E113.0")}),-1.0]])]});
            var Q2;
            Q2=makeQuery(id+"F9.imprint","IMPRINT",FACE,{"disambiguationData":[TD([[makeQuery(id+"F9.imprint","IMPRINT",EDGE,{"derivedFrom":sQuery(id+"F9.wireOp",EDGE,"E114.0")}),-1.0]])]});
            var Q3;
            Q3=makeQuery(id+"F9.imprint","IMPRINT",FACE,{"disambiguationData":[TD([[makeQuery(id+"F9.imprint","IMPRINT",EDGE,{"derivedFrom":sQuery(id+"F9.wireOp",EDGE,"E115.0")}),-1.0]])]});
            var Q4;
            Q4=makeQuery(id+"F9.imprint","IMPRINT",FACE,{"disambiguationData":[TD([[makeQuery(id+"F9.imprint","IMPRINT",EDGE,{"derivedFrom":sQuery(id+"F9.wireOp",EDGE,"E116.0")}),-1.0]])]});
            extrude(context, id + "F11", {"entities" : qUnion([Q0, Q1, Q2, Q3, Q4]), "operationType" : NewBodyOperationType.REMOVE, "oppositeDirection" : true, "depth" : 17 * mm});
        }
        {
            var Q0;
            Q0=makeQuery(id+"F9.imprint","IMPRINT",FACE,{"disambiguationData":[TD([[makeQuery(id+"F9.imprint","IMPRINT",EDGE,{"derivedFrom":sQuery(id+"F9.wireOp",EDGE,"E108")}),1.0]])]});
            var Q1;
            Q1=makeQuery(id+"F9.imprint","IMPRINT",FACE,{"disambiguationData":[TD([[makeQuery(id+"F9.imprint","IMPRINT",EDGE,{"derivedFrom":sQuery(id+"F9.wireOp",EDGE,"E109")}),1.0]])]});
            var Q2;
            Q2=makeQuery(id+"F9.imprint","IMPRINT",FACE,{"disambiguationData":[TD([[makeQuery(id+"F9.imprint","IMPRINT",EDGE,{"derivedFrom":sQuery(id+"F9.wireOp",EDGE,"E110")}),1.0]])]});
            var Q3;
            Q3=makeQuery(id+"F9.imprint","IMPRINT",FACE,{"disambiguationData":[TD([[makeQuery(id+"F9.imprint","IMPRINT",EDGE,{"derivedFrom":sQuery(id+"F9.wireOp",EDGE,"E111")}),1.0]])]});
            extrude(context, id + "F12", {"entities" : qUnion([Q0, Q1, Q2, Q3]), "operationType" : NewBodyOperationType.REMOVE, "oppositeDirection" : true, "depth" : 18 * mm});
        }
        {
            var Q0;
            Q0=makeQuery(id+"F12.boolean.opBoolean","COPY",FACE,{"derivedFrom":makeQuery(id+"F12.opExtrude","CAP_FACE",FACE,{"disambiguationData":[OSD([sQuery(id+"F9.wireOp",EDGE,"E111")])],"isStart":false})});
            var Q1;
            Q1=makeQuery(id+"F12.boolean.opBoolean","COPY",FACE,{"derivedFrom":makeQuery(id+"F12.opExtrude","CAP_FACE",FACE,{"disambiguationData":[OSD([sQuery(id+"F9.wireOp",EDGE,"E110")])],"isStart":false})});
            var Q2;
            Q2=makeQuery(id+"F12.boolean.opBoolean","COPY",FACE,{"derivedFrom":makeQuery(id+"F12.opExtrude","CAP_FACE",FACE,{"disambiguationData":[OSD([sQuery(id+"F9.wireOp",EDGE,"E109")])],"isStart":false})});
            var Q3;
            Q3=makeQuery(id+"F12.boolean.opBoolean","COPY",FACE,{"derivedFrom":makeQuery(id+"F12.opExtrude","CAP_FACE",FACE,{"disambiguationData":[OSD([sQuery(id+"F9.wireOp",EDGE,"E108")])],"isStart":false})});
            var Q4;
            Q4=makeQuery(id+"F10.boolean.opBoolean","COPY",FACE,{"derivedFrom":makeQuery(id+"F10.opExtrude","CAP_FACE",FACE,{"disambiguationData":[OSD([sQuery(id+"F9.wireOp",EDGE,"E106")])],"isStart":false})});
            var Q5;
            Q5=makeQuery(id+"F10.boolean.opBoolean","COPY",FACE,{"derivedFrom":makeQuery(id+"F10.opExtrude","CAP_FACE",FACE,{"disambiguationData":[OSD([sQuery(id+"F9.wireOp",EDGE,"E107")])],"isStart":false})});
            var Q6;
            Q6=makeQuery(id+"F10.boolean.opBoolean","COPY",FACE,{"derivedFrom":makeQuery(id+"F10.opExtrude","CAP_FACE",FACE,{"disambiguationData":[OSD([sQuery(id+"F9.wireOp",EDGE,"E105")])],"isStart":false})});
            var Q7;
            Q7=makeQuery(id+"F10.boolean.opBoolean","COPY",FACE,{"derivedFrom":makeQuery(id+"F10.opExtrude","CAP_FACE",FACE,{"disambiguationData":[OSD([sQuery(id+"F9.wireOp",EDGE,"E104")])],"isStart":false})});
            var Q8;
            Q8=makeQuery(id+"F10.boolean.opBoolean","COPY",FACE,{"derivedFrom":makeQuery(id+"F10.opExtrude","CAP_FACE",FACE,{"disambiguationData":[OSD([sQuery(id+"F9.wireOp",EDGE,"E103")])],"isStart":false})});
            extrude(context, id + "F13", {"entities" : qUnion([Q0, Q1, Q2, Q3, Q4, Q5, Q6, Q7, Q8]), "operationType" : NewBodyOperationType.REMOVE, "oppositeDirection" : true, "depth" : 9 * mm, "hasDraft" : true, "draftAngle" : 45 * degree, "draftPullDirection" : true});
        }
        {
            var Q0;
            Q0=makeQuery(id+"F11.boolean.opBoolean","COPY",FACE,{"derivedFrom":makeQuery(id+"F11.opExtrude","CAP_FACE",FACE,{"disambiguationData":[OSD([sQuery(id+"F9.wireOp",EDGE,"E116.0"),sQuery(id+"F9.wireOp",EDGE,"E116.1"),sQuery(id+"F9.wireOp",EDGE,"E116.2"),sQuery(id+"F9.wireOp",EDGE,"E116.3")])],"isStart":false})});
            var Q1;
            Q1=makeQuery(id+"F11.boolean.opBoolean","COPY",FACE,{"derivedFrom":makeQuery(id+"F11.opExtrude","CAP_FACE",FACE,{"disambiguationData":[OSD([sQuery(id+"F9.wireOp",EDGE,"E115.0"),sQuery(id+"F9.wireOp",EDGE,"E115.1"),sQuery(id+"F9.wireOp",EDGE,"E115.2"),sQuery(id+"F9.wireOp",EDGE,"E115.3")])],"isStart":false})});
            var Q2;
            Q2=makeQuery(id+"F11.boolean.opBoolean","COPY",FACE,{"derivedFrom":makeQuery(id+"F11.opExtrude","CAP_FACE",FACE,{"disambiguationData":[OSD([sQuery(id+"F9.wireOp",EDGE,"E114.0"),sQuery(id+"F9.wireOp",EDGE,"E114.1"),sQuery(id+"F9.wireOp",EDGE,"E114.2"),sQuery(id+"F9.wireOp",EDGE,"E114.3")])],"isStart":false})});
            var Q3;
            Q3=makeQuery(id+"F11.boolean.opBoolean","COPY",FACE,{"derivedFrom":makeQuery(id+"F11.opExtrude","CAP_FACE",FACE,{"disambiguationData":[OSD([sQuery(id+"F9.wireOp",EDGE,"E113.0"),sQuery(id+"F9.wireOp",EDGE,"E113.1"),sQuery(id+"F9.wireOp",EDGE,"E113.2"),sQuery(id+"F9.wireOp",EDGE,"E113.3")])],"isStart":false})});
            var Q4;
            Q4=makeQuery(id+"F11.boolean.opBoolean","COPY",FACE,{"derivedFrom":makeQuery(id+"F11.opExtrude","CAP_FACE",FACE,{"disambiguationData":[OSD([sQuery(id+"F7.wireOp",EDGE,"E71.3"),sQuery(id+"F9.wireOp",EDGE,"E112.0"),sQuery(id+"F9.wireOp",EDGE,"E112.1"),sQuery(id+"F9.wireOp",EDGE,"E112.2"),sQuery(id+"F9.wireOp",EDGE,"E112.3")])],"isStart":false})});
            extrude(context, id + "F14", {"entities" : qUnion([Q0, Q1, Q2, Q3, Q4]), "operationType" : NewBodyOperationType.REMOVE, "oppositeDirection" : true, "depth" : 7 * mm, "hasDraft" : true, "draftAngle" : 45 * degree, "draftPullDirection" : true});
        }
        {
            var Q0;
            Q0=qCreatedBy(makeId("Right.planeOp"),FACE);
            var sketch = newSketch(context, id + "F15", { "sketchPlane" : qUnion([Q0])});
            skPoint(sketch, "E117.0", {"position": v(-0.54, 0) * mm});
            skPoint(sketch, "E118.0", {"position": v(-0.54, -36) * mm});
            skLineSegment(sketch, "E119", {"start": v(-0.54, -36) * mm, "end": v(-0.54, -16) * mm});
            skLineSegment(sketch, "E120", {"start": v(5.46, -9) * mm, "end": v(-0.54, -3) * mm});
            skLineSegment(sketch, "E121", {"start": v(-0.54, -3) * mm, "end": v(-0.54, 0) * mm});
            skLineSegment(sketch, "E122", {"start": v(-20.36, 0) * mm, "end": v(-20.36, -36) * mm});
            skLineSegment(sketch, "E123", {"start": v(-20.36, -36) * mm, "end": v(-0.54, -36) * mm});
            skLineSegment(sketch, "E124", {"start": v(-0.54, 0) * mm, "end": v(-20.36, 0) * mm});
            skLineSegment(sketch, "E125", {"start": v(5.46, -9) * mm, "end": v(5.46, -14) * mm});
            skLineSegment(sketch, "E126", {"start": v(5.46, -14) * mm, "end": v(-0.54, -16) * mm});
            skPoint(sketch, "E127.0", {"position": v(36.66, -16) * mm});
            skSolve(sketch);
        }
        {
            var Q0;
            Q0=makeQuery(id+"F15.imprint","IMPRINT",FACE,{"disambiguationData":[TD([[makeQuery(id+"F15.imprint","IMPRINT",EDGE,{"derivedFrom":sQuery(id+"F15.wireOp",EDGE,"E119")}),1.0]])]});
            var Q1;
            Q1 = qConstructionFilter(qBodyType(qCreatedBy(id + "F15" ,EDGE), BodyType.WIRE), ConstructionObject.NO);
            extrude(context, id + "F16", {"entities" : qUnion([Q0]), "operationType" : NewBodyOperationType.REMOVE, "surfaceEntities" : qUnion([Q1]), "endBound" : BoundingType.SYMMETRIC, "depth" : 30 * mm});
        }
        {
            var Q0;
            Q0=makeQuery(id+"F16.boolean.opBoolean","COPY",FACE,{"derivedFrom":makeQuery(id+"F16.opExtrude","SWEPT_FACE",FACE,{"disambiguationData":[OSD([sQuery(id+"F15.wireOp",EDGE,"E126")])]})});
            var sketch = newSketch(context, id + "F17", { "sketchPlane" : qUnion([Q0])});
            skLineSegment(sketch, "E128.0", {"start": v(15, 0.76) * mm, "end": v(-15, 0.76) * mm, "construction": true});
            skLineSegment(sketch, "E129", {"start": v(-6.61, -2.4) * mm, "end": v(-4.88, -1.4) * mm});
            skPoint(sketch, "E129.startSnap0", {"position": v(-0.28, -2.4) * mm});
            skLineSegment(sketch, "E130", {"start": v(-4.88, -1.4) * mm, "end": v(-4.88, -3.4) * mm});
            skLineSegment(sketch, "E131", {"start": v(-4.88, -3.4) * mm, "end": v(-6.61, -2.4) * mm});
            skLineSegment(sketch, "E132", {"start": v(-4.88, -3.4) * mm, "end": v(-6.61, -3.4) * mm, "construction": true});
            skPoint(sketch, "E133", {"position": v(-5.75, -3.4) * mm});
            skLineSegment(sketch, "E134", {"start": v(-12.44, -4.8) * mm, "end": v(-9.61, -3.8) * mm});
            skLineSegment(sketch, "E135", {"start": v(-9.61, -3.8) * mm, "end": v(-10.95, -0.02) * mm});
            skLineSegment(sketch, "E136", {"start": v(-10.95, -0.02) * mm, "end": v(-13.78, -1.02) * mm});
            skLineSegment(sketch, "E137", {"start": v(-13.78, -1.02) * mm, "end": v(-12.44, -4.8) * mm});
            skLineSegment(sketch, "E138", {"start": v(-13.78, -1.02) * mm, "end": v(-9.61, -3.8) * mm, "construction": true});
            skPoint(sketch, "E139", {"position": v(-11.7, -2.4) * mm});
            skLineSegment(sketch, "E140", {"start": v(-9.61, -3.8) * mm, "end": v(-9.61, -2.4) * mm, "construction": true});
            skLineSegment(sketch, "E141", {"start": v(-9.61, -2.4) * mm, "end": v(-6.61, -2.4) * mm, "construction": true});
            skLineSegment(sketch, "E142", {"start": v(-0.28, -2.4) * mm, "end": v(-0.28, -5.57) * mm, "construction": true});
            skLineSegment(sketch, "E143", {"start": v(-0.28, -2.4) * mm, "end": v(-0.28, 0.76) * mm, "construction": true});
            skLineSegment(sketch, "E144", {"start": v(-4.88, -2.4) * mm, "end": v(-0.28, -2.4) * mm, "construction": true});
            skSolve(sketch);
        }
        {
            var Q0;
            Q0=makeQuery(id+"F0.imprint","IMPRINT",FACE,{"disambiguationData":[TD([[makeQuery(id+"F0.imprint","IMPRINT",EDGE,{"derivedFrom":sQuery(id+"F0.wireOp",EDGE,"E52")}),-1.0]])]});
            var Q1;
            Q1=makeQuery(id+"F0.imprint","IMPRINT",FACE,{"disambiguationData":[TD([[makeQuery(id+"F0.imprint","IMPRINT",EDGE,{"derivedFrom":sQuery(id+"F0.wireOp",EDGE,"E55")}),-1.0]])]});
            var Q2;
            Q2=makeQuery(id+"F0.imprint","IMPRINT",FACE,{"disambiguationData":[TD([[makeQuery(id+"F0.imprint","IMPRINT",EDGE,{"derivedFrom":sQuery(id+"F0.wireOp",EDGE,"E58")}),-1.0]])]});
            var Q3;
            Q3=makeQuery(id+"F17.imprint","IMPRINT",FACE,{"disambiguationData":[TD([[makeQuery(id+"F17.imprint","IMPRINT",EDGE,{"derivedFrom":sQuery(id+"F17.wireOp",EDGE,"E129")}),-1.0]])]});
            extrude(context, id + "F18", {"entities" : qUnion([Q0, Q1, Q2, Q3]), "operationType" : NewBodyOperationType.ADD, "depth" : 0.8 * mm, "offsetDistance" : 25 * mm});
        }
        {
            var Q0;
            Q0=makeQuery(id+"F17.imprint","IMPRINT",FACE,{"disambiguationData":[TD([[makeQuery(id+"F17.imprint","IMPRINT",EDGE,{"derivedFrom":sQuery(id+"F17.wireOp",EDGE,"E134")}),1.0]])]});
            extrude(context, id + "F19", {"entities" : qUnion([Q0]), "operationType" : NewBodyOperationType.ADD, "depth" : 0.6 * mm});
        }
        {
            var Q0;
            Q0=makeQuery(id+"F19.opExtrude","SWEPT_EDGE",EDGE,{"disambiguationData":[OSD([sQuery(id+"F17.wireOp",EDGE,"E134"),sQuery(id+"F17.wireOp",EDGE,"E137")])]});
            var Q1;
            Q1=makeQuery(id+"F19.opExtrude","SWEPT_EDGE",EDGE,{"disambiguationData":[OSD([sQuery(id+"F17.wireOp",EDGE,"E134"),sQuery(id+"F17.wireOp",EDGE,"E135")])]});
            var Q2;
            Q2=makeQuery(id+"F19.opExtrude","SWEPT_EDGE",EDGE,{"disambiguationData":[OSD([sQuery(id+"F17.wireOp",EDGE,"E136"),sQuery(id+"F17.wireOp",EDGE,"E137")])]});
            var Q3;
            Q3=makeQuery(id+"F19.opExtrude","SWEPT_EDGE",EDGE,{"disambiguationData":[OSD([sQuery(id+"F17.wireOp",EDGE,"E135"),sQuery(id+"F17.wireOp",EDGE,"E136")])]});
            fillet(context, id + "F20", {"entities" : qUnion([Q0, Q1, Q2, Q3]), "radius" : 0.5 * mm, "tangentPropagation" : true, "allowEdgeOverflow" : false});
        }
        {
            var Q0;
            Q0=makeQuery(id+"F0.imprint","IMPRINT",FACE,{"disambiguationData":[TD([[makeQuery(id+"F0.imprint","IMPRINT",EDGE,{"derivedFrom":sQuery(id+"F0.wireOp",EDGE,"E47")}),1.0]])]});
            var Q1;
            Q1=makeQuery(id+"F0.imprint","IMPRINT",FACE,{"disambiguationData":[TD([[makeQuery(id+"F0.imprint","IMPRINT",EDGE,{"derivedFrom":sQuery(id+"F0.wireOp",EDGE,"E49")}),1.0]])]});
            var Q2;
            Q2=makeQuery(id+"F0.imprint","IMPRINT",FACE,{"disambiguationData":[TD([[makeQuery(id+"F0.imprint","IMPRINT",EDGE,{"derivedFrom":sQuery(id+"F0.wireOp",EDGE,"E46")}),1.0]])]});
            extrude(context, id + "F21", {"entities" : qUnion([Q0, Q1, Q2]), "operationType" : NewBodyOperationType.ADD, "depth" : 0.6 * mm});
        }
        {
            var Q0;
            Q0=makeQuery(id+"F8.boolean.opBoolean","SPLIT",FACE,{"disambiguationData":[TD([makeQuery(id+"F8.opExtrude","SWEPT_FACE",FACE,{"disambiguationData":[OSD([sQuery(id+"F7.wireOp",EDGE,"E71.0")])]})])],"derivedFrom":makeQuery(id+"F1.opExtrude","CAP_FACE",FACE,{"disambiguationData":[OSD([sQuery(id+"F0.wireOp",EDGE,"E17"),sQuery(id+"F0.wireOp",EDGE,"E18"),sQuery(id+"F0.wireOp",EDGE,"E19"),sQuery(id+"F0.wireOp",EDGE,"E20"),sQuery(id+"F0.wireOp",EDGE,"E21.trimOffspring"),sQuery(id+"F0.wireOp",EDGE,"E39"),sQuery(id+"F0.wireOp",EDGE,"E40.trimOffspring"),sQuery(id+"F0.wireOp",EDGE,"E41.trimOffspring")])],"isStart":false})});
            var sketch = newSketch(context, id + "F22", { "sketchPlane" : qUnion([Q0])});
            skPoint(sketch, "E145.0", {"position": v(42.95, -12.46) * mm});
            skPoint(sketch, "E146.0", {"position": v(32.95, -41.16) * mm});
            skArc(sketch, "E147", {"start": v(50.46, -15.24) * mm, "mid": v(45.59, -4.9) * mm, "end": v(35.35, -9.98) * mm});
            skArc(sketch, "E148", {"start": v(25.92, -38.87) * mm, "mid": v(30.52, -48.15) * mm, "end": v(39.9, -43.74) * mm});
            skLineSegment(sketch, "E149", {"start": v(25.92, -38.87) * mm, "end": v(35.35, -9.98) * mm});
            skLineSegment(sketch, "E150", {"start": v(39.9, -43.74) * mm, "end": v(50.46, -15.24) * mm});
            skPoint(sketch, "E151.0", {"position": v(20.95, -40.84) * mm});
            skPoint(sketch, "E152.0", {"position": v(22.69, -39.84) * mm});
            skPoint(sketch, "E153.0", {"position": v(22.69, -41.84) * mm});
            skPoint(sketch, "E154.0", {"position": v(26.83, -26.81) * mm});
            skPoint(sketch, "E155.0", {"position": v(28.57, -25.81) * mm});
            skPoint(sketch, "E156.0", {"position": v(28.57, -27.81) * mm});
            skPoint(sketch, "E157.0", {"position": v(33.7, -12.46) * mm});
            skPoint(sketch, "E158.0", {"position": v(35.44, -11.46) * mm});
            skPoint(sketch, "E159.0", {"position": v(35.44, -13.46) * mm});
            skLineSegment(sketch, "E160", {"start": v(20.95, -40.84) * mm, "end": v(22.1, -40.84) * mm, "construction": true});
            skLineSegment(sketch, "E161", {"start": v(22.1, -40.84) * mm, "end": v(22.69, -39.84) * mm, "construction": true});
            skLineSegment(sketch, "E162", {"start": v(22.69, -41.84) * mm, "end": v(22.1, -40.84) * mm, "construction": true});
            skLineSegment(sketch, "E163", {"start": v(26.83, -26.81) * mm, "end": v(27.99, -26.81) * mm, "construction": true});
            skLineSegment(sketch, "E164", {"start": v(27.99, -26.81) * mm, "end": v(28.57, -25.81) * mm, "construction": true});
            skLineSegment(sketch, "E165", {"start": v(27.99, -26.81) * mm, "end": v(28.57, -27.81) * mm, "construction": true});
            skLineSegment(sketch, "E166", {"start": v(33.7, -12.46) * mm, "end": v(34.86, -12.46) * mm, "construction": true});
            skLineSegment(sketch, "E167", {"start": v(34.86, -12.46) * mm, "end": v(35.44, -13.46) * mm, "construction": true});
            skLineSegment(sketch, "E168", {"start": v(35.44, -11.46) * mm, "end": v(34.86, -12.46) * mm, "construction": true});
            skCircle(sketch, "E169", {"center": v(22.1, -40.84) * mm, "radius": 1.6 * mm});
            skCircle(sketch, "E170", {"center": v(27.99, -26.81) * mm, "radius": 1.6 * mm});
            skCircle(sketch, "E171", {"center": v(34.86, -12.46) * mm, "radius": 1.6 * mm});
            skSolve(sketch);
        }
        {
            var Q0;
            {var subQ0=sQuery(id+"F22.wireOp",EDGE,"E171");var subQ1=sQuery(id+"F22.wireOp",EDGE,"E149");var subQ2=makeQuery(id+"F22.imprint","INTERSECT",VERTEX,{"disambiguationData":[OD(0.0)],"derivedFrom":[subQ1,subQ0]});Q0=makeQuery(id+"F22.imprint","IMPRINT",FACE,{"disambiguationData":[TD([[makeQuery(id+"F22.imprint","IMPRINT",EDGE,{"disambiguationData":[TD([[subQ2,-1.0]])],"derivedFrom":subQ1}),1.0]])]});}
            var Q1;
            {var subQ0=sQuery(id+"F22.wireOp",EDGE,"E171");var subQ1=sQuery(id+"F22.wireOp",EDGE,"E149");var subQ2=makeQuery(id+"F22.imprint","INTERSECT",VERTEX,{"disambiguationData":[OD(0.0)],"derivedFrom":[subQ1,subQ0]});Q1=makeQuery(id+"F22.imprint","IMPRINT",FACE,{"disambiguationData":[TD([[makeQuery(id+"F22.imprint","IMPRINT",EDGE,{"disambiguationData":[TD([[subQ2,-1.0]])],"derivedFrom":subQ1}),-1.0]])]});}
            var Q2;
            Q2=makeQuery(id+"F22.imprint","IMPRINT",FACE,{"disambiguationData":[TD([[makeQuery(id+"F22.imprint","IMPRINT",EDGE,{"derivedFrom":sQuery(id+"F22.wireOp",EDGE,"E170")}),1.0]])]});
            var Q3;
            Q3=makeQuery(id+"F22.imprint","IMPRINT",FACE,{"disambiguationData":[TD([[makeQuery(id+"F22.imprint","IMPRINT",EDGE,{"derivedFrom":sQuery(id+"F22.wireOp",EDGE,"E169")}),1.0]])]});
            extrude(context, id + "F23", {"entities" : qUnion([Q0, Q1, Q2, Q3]), "operationType" : NewBodyOperationType.REMOVE, "oppositeDirection" : true, "depth" : 2 * mm});
        }
        {
            var Q0;
            Q0=makeQuery(id+"F23.boolean.opBoolean","COPY",FACE,{"derivedFrom":makeQuery(id+"F23.opExtrude","CAP_FACE",FACE,{"disambiguationData":[OSD([sQuery(id+"F22.wireOp",EDGE,"E171")])],"isStart":false})});
            var Q1;
            Q1=makeQuery(id+"F23.boolean.opBoolean","COPY",FACE,{"derivedFrom":makeQuery(id+"F23.opExtrude","CAP_FACE",FACE,{"disambiguationData":[OSD([sQuery(id+"F22.wireOp",EDGE,"E170")])],"isStart":false})});
            var Q2;
            Q2=makeQuery(id+"F23.boolean.opBoolean","COPY",FACE,{"derivedFrom":makeQuery(id+"F23.opExtrude","CAP_FACE",FACE,{"disambiguationData":[OSD([sQuery(id+"F22.wireOp",EDGE,"E169")])],"isStart":false})});
            extrude(context, id + "F24", {"entities" : qUnion([Q0, Q1, Q2]), "operationType" : NewBodyOperationType.REMOVE, "oppositeDirection" : true, "depth" : 5 * mm, "hasDraft" : true, "draftAngle" : 45 * degree, "draftPullDirection" : true});
        }
        {
            var Q0;
            {var subQ1=sQuery(id+"F22.wireOp",EDGE,"E147");Q0=makeQuery(id+"F22.imprint","IMPRINT",FACE,{"disambiguationData":[TD([[makeQuery(id+"F22.imprint","IMPRINT",EDGE,{"derivedFrom":subQ1}),1.0]])]});}
            var Q1;
            {var subQ0=sQuery(id+"F22.wireOp",EDGE,"E171");var subQ1=sQuery(id+"F22.wireOp",EDGE,"E149");var subQ2=makeQuery(id+"F22.imprint","INTERSECT",VERTEX,{"disambiguationData":[OD(0.0)],"derivedFrom":[subQ1,subQ0]});Q1=makeQuery(id+"F22.imprint","IMPRINT",FACE,{"disambiguationData":[TD([[makeQuery(id+"F22.imprint","IMPRINT",EDGE,{"disambiguationData":[TD([[subQ2,-1.0]])],"derivedFrom":subQ1}),-1.0]])]});}
            extrude(context, id + "F25", {"entities" : qUnion([Q0, Q1]), "operationType" : NewBodyOperationType.REMOVE, "oppositeDirection" : true, "depth" : 15 * mm});
        }
        {
            var Q0;
            Q0=makeQuery(id+"F25.boolean.opBoolean","COPY",FACE,{"derivedFrom":makeQuery(id+"F25.opExtrude","CAP_FACE",FACE,{"disambiguationData":[OSD([sQuery(id+"F22.wireOp",EDGE,"E147"),sQuery(id+"F22.wireOp",EDGE,"E148"),sQuery(id+"F22.wireOp",EDGE,"E149"),sQuery(id+"F22.wireOp",EDGE,"E150")])],"isStart":false})});
            extrude(context, id + "F26", {"entities" : qUnion([Q0]), "operationType" : NewBodyOperationType.REMOVE, "oppositeDirection" : true, "depth" : 25 * mm, "hasDraft" : true, "draftAngle" : 54 * degree, "draftPullDirection" : true});
        }
        {
            var Q0;
            Q0=makeQuery(id+"F19.opExtrude","CAP_FACE",FACE,{"disambiguationData":[OSD([sQuery(id+"F17.wireOp",EDGE,"E134"),sQuery(id+"F17.wireOp",EDGE,"E135"),sQuery(id+"F17.wireOp",EDGE,"E136"),sQuery(id+"F17.wireOp",EDGE,"E137")])],"isStart":false});
            var sketch = newSketch(context, id + "F27", { "sketchPlane" : qUnion([Q0])});
            skLineSegment(sketch, "E172", {"start": v(-11.42, -0.19) * mm, "end": v(-11.97, -4.63) * mm, "construction": true});
            skCircle(sketch, "E173", {"center": v(-11.7, -2.4) * mm, "radius": 1.1 * mm});
            skCircle(sketch, "E174", {"center": v(-11.7, -2.4) * mm, "radius": 0.3 * mm});
            skSolve(sketch);
        }
        {
            var Q0;
            Q0=makeQuery(id+"F27.imprint","IMPRINT",FACE,{"disambiguationData":[TD([[makeQuery(id+"F27.imprint","IMPRINT",EDGE,{"derivedFrom":sQuery(id+"F27.wireOp",EDGE,"E173")}),1.0]])]});
            extrude(context, id + "F28", {"entities" : qUnion([Q0]), "operationType" : NewBodyOperationType.REMOVE, "oppositeDirection" : true, "depth" : 0.2 * mm});
        }
        {
            var Q0;
            Q0=makeQuery(id+"F8.boolean.opBoolean","COPY",EDGE,{"derivedFrom":makeQuery(id+"F8.opExtrude","CAP_EDGE",EDGE,{"disambiguationData":[OSD([sQuery(id+"F7.wireOp",EDGE,"E70.2")])],"isStart":false})});
            var Q1;
            Q1=makeQuery(id+"F8.boolean.opBoolean","COPY",EDGE,{"derivedFrom":makeQuery(id+"F8.opExtrude","CAP_EDGE",EDGE,{"disambiguationData":[OSD([sQuery(id+"F7.wireOp",EDGE,"E71.2")])],"isStart":false})});
            fillet(context, id + "F29", {"entities" : qUnion([Q0, Q1]), "radius" : 1.2 * mm, "tangentPropagation" : true, "allowEdgeOverflow" : false});
        }
        {
            var Q0;
            Q0=makeQuery(id+"F6.opExtrude","CAP_EDGE",EDGE,{"disambiguationData":[OSD([sQuery(id+"F5.wireOp",EDGE,"E67.5")])],"isStart":false});
            var Q1;
            Q1=makeQuery(id+"F6.opExtrude","CAP_EDGE",EDGE,{"disambiguationData":[OSD([sQuery(id+"F5.wireOp",EDGE,"E66.5")])],"isStart":false});
            fillet(context, id + "F30", {"entities" : qUnion([Q0, Q1]), "radius" : 0.4 * mm, "tangentPropagation" : true, "allowEdgeOverflow" : false});
        }
    });
